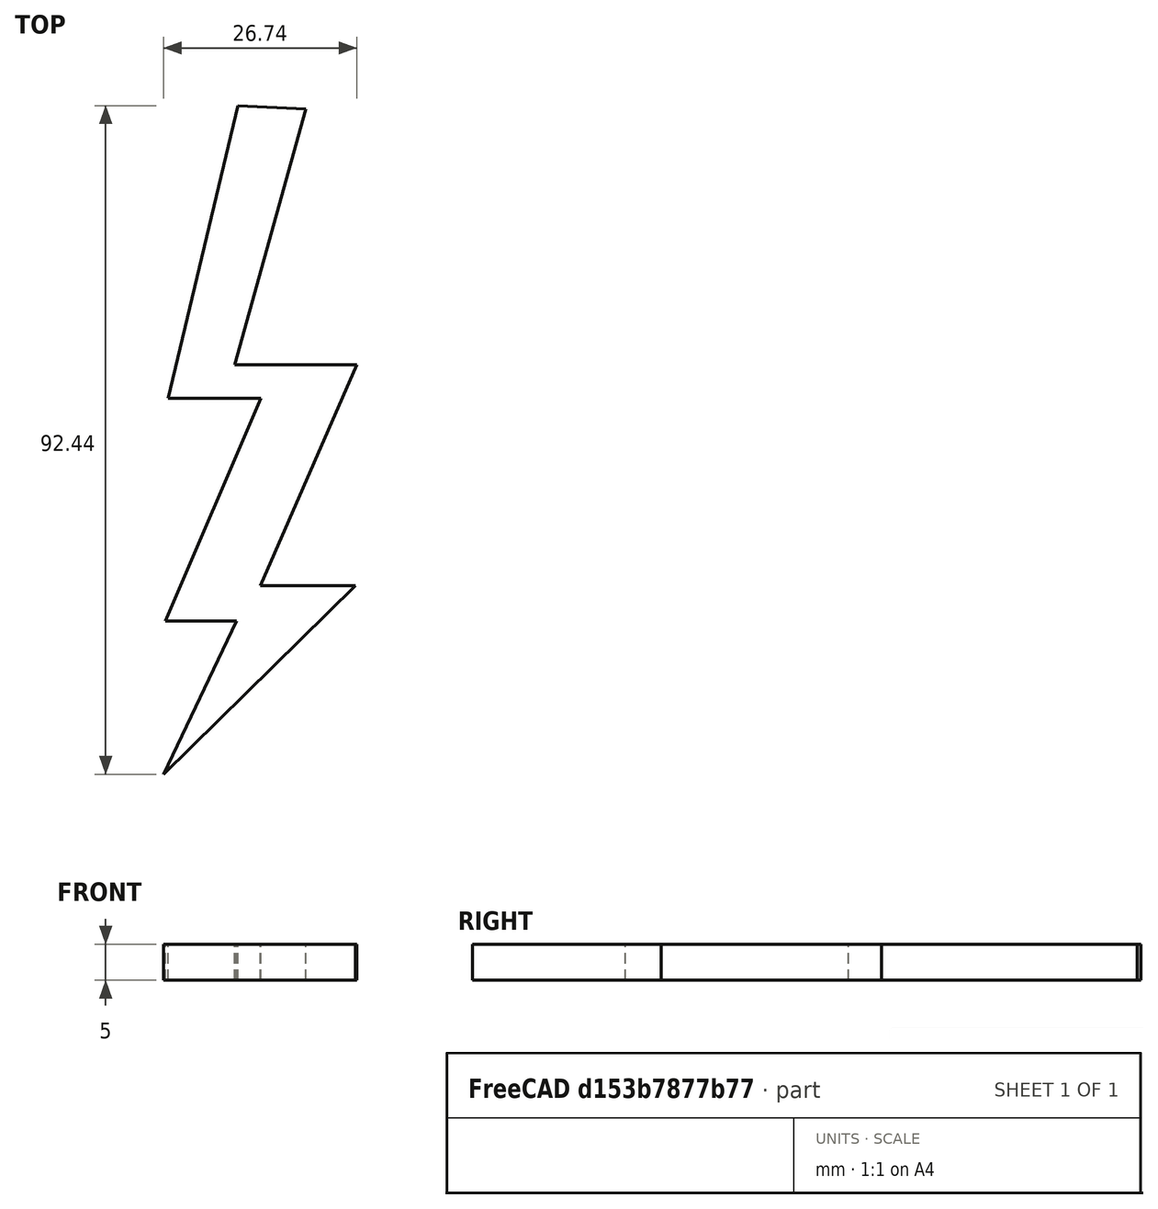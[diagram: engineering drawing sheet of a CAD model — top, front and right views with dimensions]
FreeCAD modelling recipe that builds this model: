
FCSTD DOCUMENT  (FreeCAD 0.21R33694 (Git))
Label: OJT1_T016_Llamp
License: All rights reserved
LicenseURL: https://en.wikipedia.org/wiki/All_rights_reserved
objects: Sketcher::SketchObject×1, PartDesign::Pad×1, PartDesign::Body×1
note: 4 computed .brp shape members not serialized (recipe doc carries the construction recipe); baked Part::Feature solids carry a one-line shape summary decoded from their .brp

FEATURE [Sketcher::SketchObject] Sketch
  FullyConstrained = false
  MapMode = 5
  Support = -> [XY_Plane]
  sketch-geometry (11):
    g0: LineSegment StartX=19.8287 StartY=49.9522 StartZ=0 EndX=10.1879 EndY=9.49855 EndZ=0
    g1: LineSegment StartX=10.1879 StartY=9.49855 StartZ=0 EndX=23.0423 EndY=9.49855 EndZ=0
    g2: LineSegment StartX=23.0423 StartY=9.49855 StartZ=0 EndX=9.80983 EndY=-21.3143 EndZ=0
    g3: LineSegment StartX=9.80983 StartY=-21.3143 StartZ=0 EndX=19.6397 EndY=-21.3143 EndZ=0
    g4: LineSegment StartX=19.6397 StartY=-21.3143 StartZ=0 EndX=9.54393 EndY=-42.4893 EndZ=0
    g5: LineSegment StartX=9.54393 StartY=-42.4893 StartZ=0 EndX=36.0962 EndY=-16.3988 EndZ=0
    g6: LineSegment StartX=36.0962 StartY=-16.3988 StartZ=0 EndX=22.9355 EndY=-16.3988 EndZ=0
    g7: LineSegment StartX=22.9355 StartY=-16.3988 StartZ=0 EndX=36.2803 EndY=14.1253 EndZ=0
    g8: LineSegment StartX=36.2803 StartY=14.1253 StartZ=0 EndX=19.3927 EndY=14.1253 EndZ=0
    g9: LineSegment StartX=19.3927 StartY=14.1253 StartZ=0 EndX=29.2111 EndY=49.4713 EndZ=0
    g10: LineSegment StartX=29.2111 StartY=49.4713 StartZ=0 EndX=19.8287 EndY=49.9522 EndZ=0
  constraints (12):
    c: Coincident(g1,g0)
    c: Horizontal(g1)
    c: Coincident(g2,g1)
    c: Coincident(g3,g2)
    c: Horizontal(g3)
    c: Coincident(g4,g3)
    c: Coincident(g5,g4)
    c: Coincident(g6,g5)
    c: Horizontal(g6)
    c: Coincident(g7,g6)
    c: Horizontal(g8)
    c: Coincident(g10,g0)
FEATURE [PartDesign::Pad] Pad
  Direction = (0,0,1)
  Length = 5
  Length2 = 10
  Profile = -> Sketch
  ReferenceAxis = -> Sketch [N_Axis]
  Type = 0
FEATURE [PartDesign::Body] Body
  Group = -> [Sketch,Pad]
  Origin = -> Origin
  Tip = -> Pad
